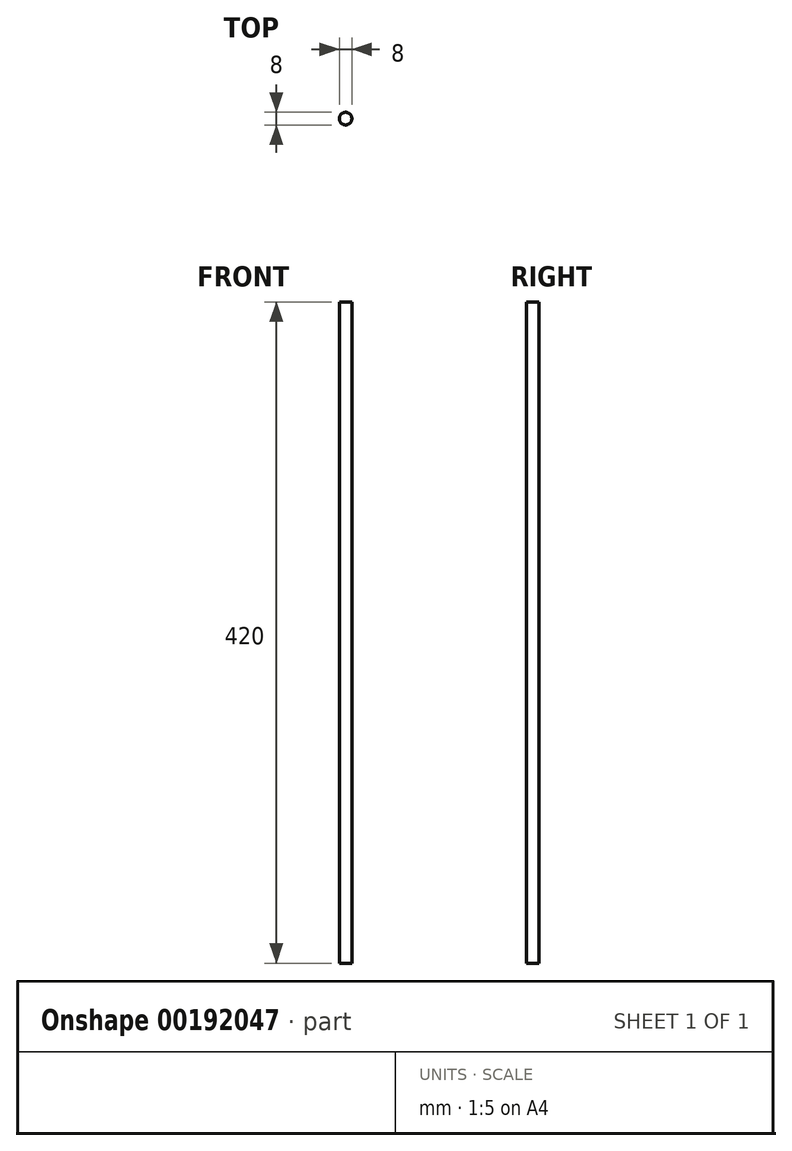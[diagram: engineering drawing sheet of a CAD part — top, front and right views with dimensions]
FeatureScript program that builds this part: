
annotation { "Feature Type Name" : "Feature", "Feature Type Description" : "" }
export const myFeature = defineFeature(function(context is Context, id is Id, definition is map)
    precondition{}
    {
        {
            var Q0;
            Q0=qCreatedBy(makeId("Top.planeOp"),FACE);
            var sketch = newSketch(context, id + "F0", { "sketchPlane" : qUnion([Q0])});
            skCircle(sketch, "E0", {"center": v(0, 0) * mm, "radius": 4 * mm});
            skSolve(sketch);
        }
        {
            var Q0;
            Q0 = qSketchRegion(id + "F0", true);
            extrude(context, id + "F1", {"entities" : qUnion([Q0]), "depth" : (360 + 30 + 30) * mm});
        }
    });
